# Revit family: Deca_Barra lateral fixa 30 cm_Conforto_2373.030
name_source: partatom
category: Plumbing Fixtures
units: mm (PartAtom-declared; Revit-internal decimal feet)

## family parameters
Cut with Voids When Loaded = No
Host = Face
Part Type = Normal
Room Calculation Point = No
Round Connector Dimension = Use Diameter
Shared = No

## types (1)
- 2373.I.030.POL_Aço Polido
    Acompanha o Produto = Acompanha Parafusos e Buchas para fixação para alvenaria
    Aprovado por = quattroD
    Atendimento ao Cliente = 0800-0117073
    Categoria = ACESSORIOS
    Composição Anel Vedação = -
    Composição Assento = -
    Composição Básica = Aço Inoxidável
    Composição Componente = -
    Consumo = -
    Cor Interna = -
    Cor Principal = Aço Polido
    Cor Secundária = -
    Cores Componente = -
    Criado por = quattroD
    Código Pai = 2373.030
    Default Elevation = 0.75 mm  [stored 0.00246063 ft]
    Description = Barra lateral fixa 30 cm
    Informações Complementares = -
    Itens de Instalação = -
    Linha = Conforto
    Manufacturer = Deca
    Material = Deca_Aço Polido
    Model = 2373.I.030.POL
    Norma = NBR9050
    Peso Líquido (Kg) = 0.417
    Pressão máx. funcionamento = -
    Pressão mín. Aquec. Acúmulo = -
    Pressão mín. Aquec. Passagem = -
    Pressão mín. funcionamento = -
    Saída de Esgoto = -
    Segmento = Banheiro Médio
    Tipo de dispositivo economizador = -
    Tipo de mecanismo utilizado = -
    Tipo de rosca de entrada = -
    Tipo de rosca de saída = -
    URL = www.deca.com.br
    Vazão na Pressão máx. (L/min) = -
    Vazão na Pressão mín. (L/min) = -

note: [stored X ft] marks values corroborated as IEEE doubles in the binary element streams (Revit-internal decimal feet)

## geometry (parser evidence)
native form markers: Sweep x2
no freeform markers — native parametric forms only
